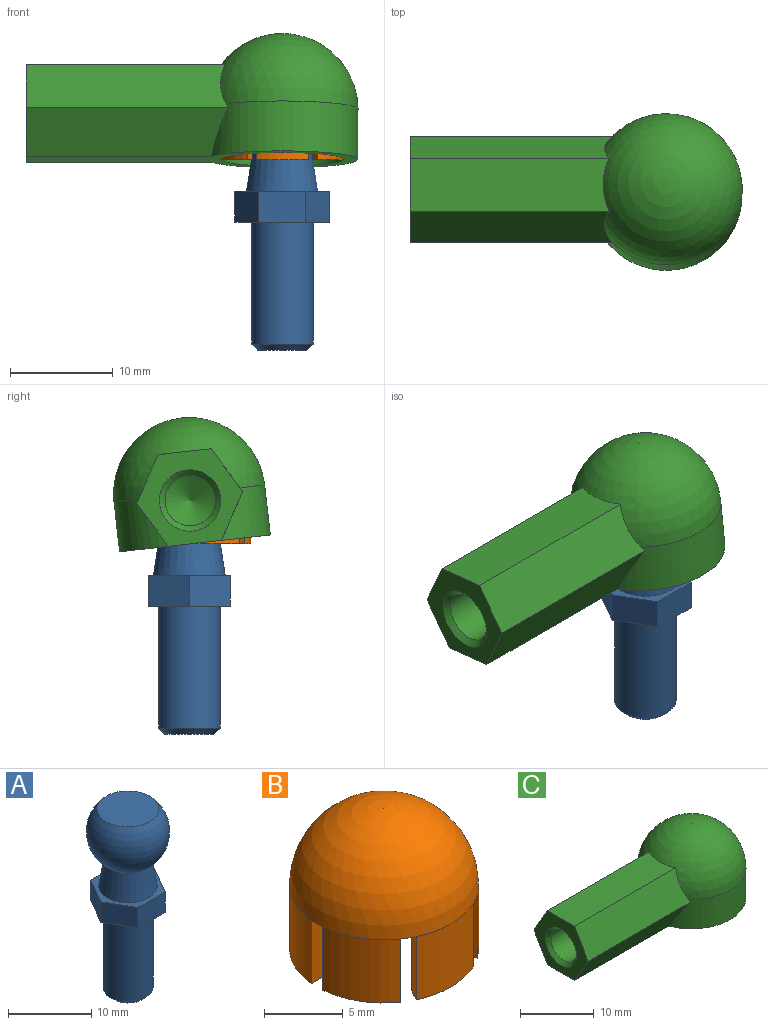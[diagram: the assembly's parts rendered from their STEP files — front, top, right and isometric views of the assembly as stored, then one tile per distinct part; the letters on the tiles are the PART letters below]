
ASSEMBLY  parts=3 mates=2
PART A: 14 faces, bbox 10x10x26.8 mm
  f0: sphere r=5mm, area 232.4mm2, adj f1,f2
  f1: cone r=2.91mm half-angle=8.5deg, axis (0,0,-1), area 80.1mm2, adj f0,f3
  f2: plane 7.46x7.46mm, normal (0,0,1), area 43.7mm2, adj f0
  f3: plane 9.24x8mm, normal (0,0,1), area 16.9mm2, adj f1,f8,f9,f10,f11,f12,f13
  f4: plane 9.24x8mm, normal (0,0,-1), area 27.2mm2, adj f5,f8,f9,f10,f11,f12,f13
  f5: cylinder r=3mm len=11.89mm, axis (0,0,1), area 224.1mm2, adj f4,f6
  f6: cone r=3mm half-angle=45deg, axis (0,0,1), area 14.7mm2, adj f5,f7
  f7: plane 4.77x4.77mm, normal (0,0,-1), area 17.9mm2, adj f6
  f8: plane 4x3mm, normal (-0.87,-0.5,0), area 13.9mm2, adj f3,f4,f9,f13
  f9: plane 4.62x3mm, normal (0,-1,0), area 13.9mm2, adj f3,f4,f8,f10
  f10: plane 4x3mm, normal (0.87,-0.5,0), area 13.9mm2, adj f3,f4,f9,f11
  f11: plane 4x3mm, normal (0.87,0.5,0), area 13.9mm2, adj f3,f4,f10,f12
  f12: plane 4.62x3mm, normal (0,1,0), area 13.9mm2, adj f3,f4,f11,f13
  f13: plane 4x3mm, normal (-0.87,0.5,0), area 13.9mm2, adj f3,f4,f8,f12
PART B: 38 faces, bbox 12x12x10.9 mm
  f0: plane 4.9x0.87mm, normal (0.87,0.5,0), area 4.9mm2, adj f11,f20,f33,f35
  f1: plane 1.03x1mm, normal (0,0,-1), area 1mm2, adj f7,f14,f28,f29
  f2: plane 4.9x0.87mm, normal (-0.87,-0.5,0), area 4.9mm2, adj f5,f6,f13,f20
  f3: cylinder r=6mm len=4.9mm, axis (0,0,1), area 25.9mm2, adj f7,f9,f15,f24
  f4: cylinder r=6mm len=4.9mm, axis (0,0,1), area 25.9mm2, adj f7,f12,f16,f17
  f5: cylinder r=6mm len=4.9mm, axis (0,0,1), area 25.9mm2, adj f2,f6,f7,f28
  f6: plane 4.43x3.06mm, normal (0,0,-1), area 4.8mm2, adj f2,f5,f13,f28
  f7: sphere r=6mm, area 226.2mm2, adj f1,f3,f4,f5,f8,f10,f11,f19
  f8: cylinder r=6mm len=5.11mm, axis (0,0,1), area 25.9mm2, adj f7,f22,f27,f30
  f9: plane 4.43x3.06mm, normal (0,0,-1), area 4.8mm2, adj f3,f15,f24,f31
  f10: cylinder r=6mm len=4.9mm, axis (0,0,1), area 25.9mm2, adj f7,f25,f29,f32
  f11: cylinder r=6mm len=5.11mm, axis (0,0,1), area 25.9mm2, adj f0,f7,f18,f33
  f12: plane 4.43x3.06mm, normal (0,0,-1), area 4.8mm2, adj f4,f16,f17,f34
  f13: cylinder r=5mm len=4.9mm, axis (0,0,1), area 20.7mm2, adj f2,f6,f14,f28
  f14: sphere r=5mm, area 157.1mm2, adj f1,f13,f19,f20,f21,f23,f26,f31
  f15: plane 4.9x1mm, normal (0,-1,0), area 4.9mm2, adj f3,f9,f21,f31
  f16: plane 4.9x1mm, normal (0,1,0), area 4.9mm2, adj f4,f12,f21,f34
  f17: plane 4.9x0.87mm, normal (0.87,-0.5,0), area 4.9mm2, adj f4,f12,f19,f34
  f18: plane 4.9x0.87mm, normal (-0.87,0.5,0), area 4.9mm2, adj f11,f19,f33,f35
  f19: plane 1.37x1.37mm, normal (0,0,-1), area 1mm2, adj f7,f14,f17,f18
  f20: plane 1.37x1.37mm, normal (0,0,-1), area 1mm2, adj f0,f2,f7,f14
  f21: plane 1.03x1mm, normal (0,0,-1), area 1mm2, adj f7,f14,f15,f16
  f22: plane 4.9x0.87mm, normal (-0.87,-0.5,0), area 4.9mm2, adj f8,f23,f30,f37
  f23: plane 1.37x1.37mm, normal (0,0,-1), area 1mm2, adj f7,f14,f22,f24
  f24: plane 4.9x0.87mm, normal (0.87,0.5,0), area 4.9mm2, adj f3,f9,f23,f31
  f25: plane 4.9x0.87mm, normal (-0.87,0.5,0), area 4.9mm2, adj f10,f26,f32,f36
  f26: plane 1.37x1.37mm, normal (0,0,-1), area 1mm2, adj f7,f14,f25,f27
  f27: plane 4.9x0.87mm, normal (0.87,-0.5,0), area 4.9mm2, adj f8,f26,f30,f37
  f28: plane 4.9x1mm, normal (0,1,0), area 4.9mm2, adj f1,f5,f6,f13
  f29: plane 4.9x1mm, normal (0,-1,0), area 4.9mm2, adj f1,f10,f32,f36
  f30: plane 5.11x1.44mm, normal (0,0,-1), area 4.8mm2, adj f8,f22,f27,f37
  f31: cylinder r=5mm len=4.9mm, axis (0,0,1), area 20.7mm2, adj f9,f14,f15,f24
  f32: plane 4.43x3.06mm, normal (0,0,-1), area 4.8mm2, adj f10,f25,f29,f36
  f33: plane 5.11x1.44mm, normal (0,0,-1), area 4.8mm2, adj f0,f11,f18,f35
  f34: cylinder r=5mm len=4.9mm, axis (0,0,1), area 20.7mm2, adj f12,f14,f16,f17
  f35: cylinder r=5mm len=4.9mm, axis (0,0,1), area 20.7mm2, adj f0,f14,f18,f33
  f36: cylinder r=5mm len=4.9mm, axis (0,0,1), area 20.7mm2, adj f14,f25,f29,f32
  f37: cylinder r=5mm len=4.9mm, axis (0,0,1), area 20.7mm2, adj f14,f22,f27,f30
PART C: 14 faces, bbox 32.4x14.8x12.3 mm
  f0: cone r=2.46mm half-angle=60deg, axis (-1,0,0), area 21.9mm2, adj f11
  f1: plane 32.4x14.8mm, normal (0,0,-1), area 151.2mm2, adj f3,f5,f6,f9,f13
  f2: plane 19.74x4.5mm, normal (0,-0.87,0.5), area 99.7mm2, adj f3,f4,f5,f8,f9
  f3: cylinder r=7.4mm len=14.8mm, axis (0,0,1), area 186.1mm2, adj f1,f2,f4,f5,f6,f7
  f4: sphere r=7.4mm, area 309.6mm2, adj f2,f3,f7,f8
  f5: plane 19.73x4.5mm, normal (0,-0.87,-0.5), area 97.5mm2, adj f1,f2,f3,f9
  f6: plane 19.73x4.5mm, normal (0,0.87,-0.5), area 97.5mm2, adj f1,f3,f7,f9
  f7: plane 19.74x4.5mm, normal (0,0.87,0.5), area 99.7mm2, adj f3,f4,f6,f8,f9
  f8: plane 19.41x5.2mm, normal (0,0,1), area 98.9mm2, adj f2,f4,f7,f9
  f9: plane 10.39x9mm, normal (-1,0,0), area 41.9mm2, adj f1,f2,f5,f6,f7,f8,f10
  f10: cone r=3mm half-angle=45deg, axis (-1,0,0), area 13.1mm2, adj f9,f11
  f11: cylinder r=2.46mm len=15.46mm, axis (-1,0,0), area 238.8mm2, adj f0,f10
  f12: sphere r=6mm, area 226.2mm2, adj f13
  f13: cylinder r=6mm len=12mm, axis (0,0,1), area 184.7mm2, adj f1,f12
PLACE A t=(-3.84,3.29,-4.11)mm
PLACE B t=(-3.84,3.29,-4.11)mm
PLACE C rot(axis=(-1,0,0),6.4deg) t=(-3.84,3.29,-4.11)mm
MATE ball B.f3 <-> C.f3  axis (0,0,1) through (-3.84,3.29,-4.11)mm
MATE ball A.f1 <-> B.f3  axis (0,0,1) through (-3.84,3.29,-4.11)mm
